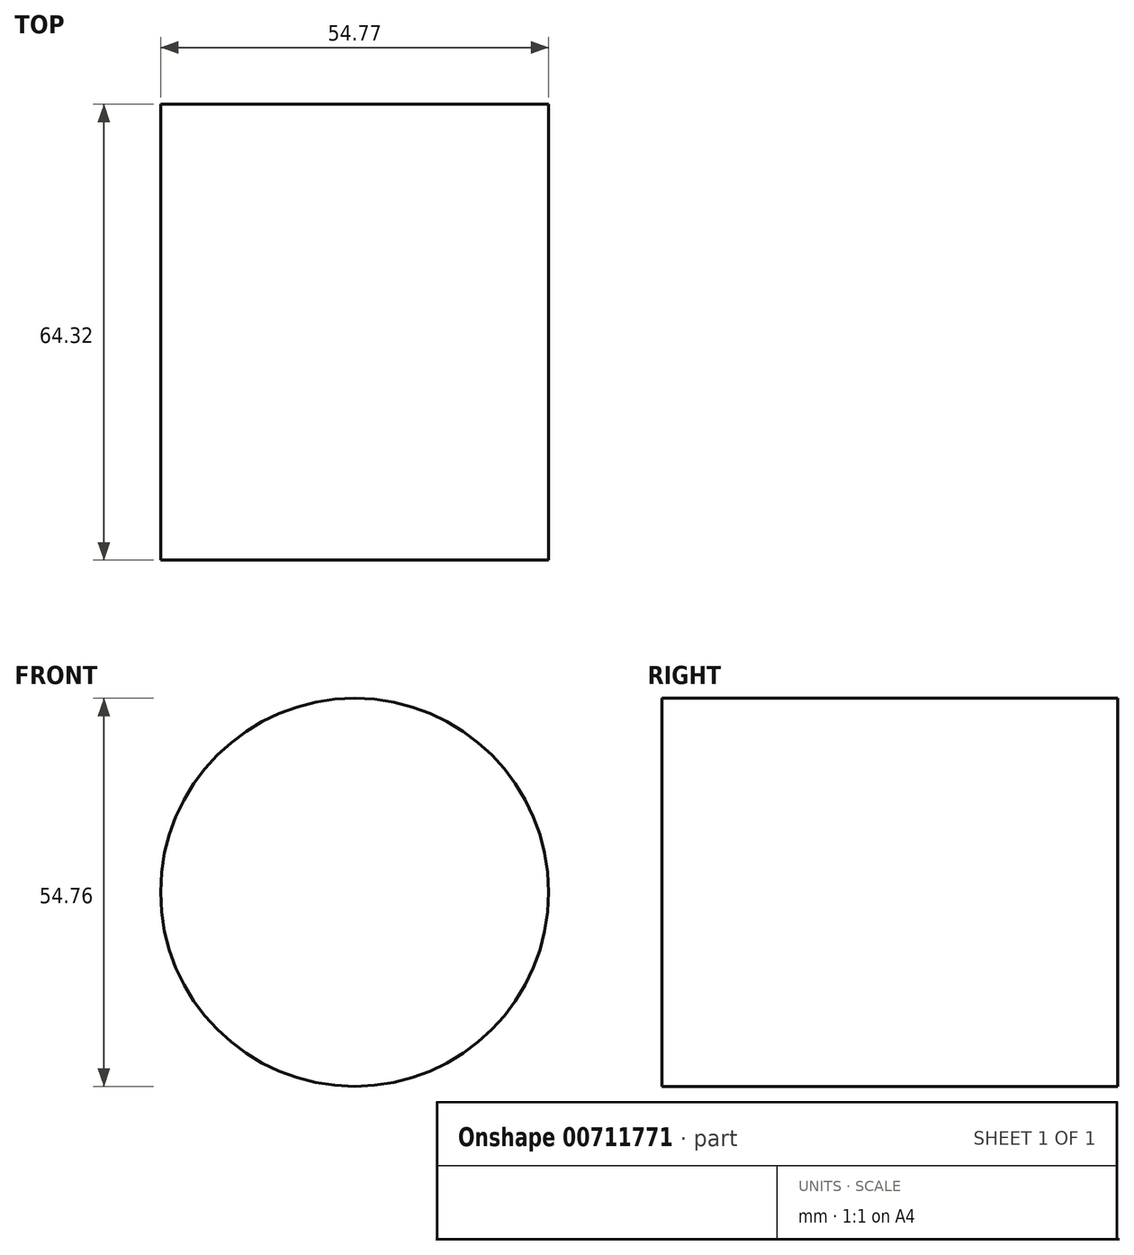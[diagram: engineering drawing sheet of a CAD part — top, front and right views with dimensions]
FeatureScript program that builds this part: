
annotation { "Feature Type Name" : "Feature", "Feature Type Description" : "" }
export const myFeature = defineFeature(function(context is Context, id is Id, definition is map)
    precondition{}
    {
        {
            var Q0;
            Q0=qCreatedBy(makeId("Top.planeOp"),FACE);
            var sketch = newSketch(context, id + "F0", { "sketchPlane" : qUnion([Q0])});
            skLineSegment(sketch, "E0.bottom", {"start": v(31.2, -24.15) * mm, "end": v(56.98, -24.15) * mm});
            skLineSegment(sketch, "E0.top", {"start": v(31.2, 44.87) * mm, "end": v(56.98, 44.87) * mm});
            skLineSegment(sketch, "E0.left", {"start": v(31.2, -24.15) * mm, "end": v(31.2, 44.87) * mm});
            skLineSegment(sketch, "E0.right", {"start": v(56.98, -24.15) * mm, "end": v(56.98, 44.87) * mm});
            skSolve(sketch);
        }
        {
            var Q0;
            Q0 = qSketchRegion(id + "F0", true);
            extrude(context, id + "F1", {"entities" : qUnion([Q0]), "depth" : 97.16 * mm, "offsetDistance" : 25.4 * mm});
        }
        {
            var Q0;
            Q0=makeQuery(id+"F1.opExtrude","SWEPT_FACE",FACE,{"disambiguationData":[OSD([sQuery(id+"F0.wireOp",EDGE,"E0.right")])]});
            var sketch = newSketch(context, id + "F2", { "sketchPlane" : qUnion([Q0])});
            skLineSegment(sketch, "E1.bottom", {"start": v(0, 81.33) * mm, "end": v(29.34, 81.33) * mm});
            skLineSegment(sketch, "E1.top", {"start": v(0, 13.33) * mm, "end": v(29.34, 13.33) * mm});
            skLineSegment(sketch, "E1.left", {"start": v(0, 81.33) * mm, "end": v(0, 13.33) * mm});
            skLineSegment(sketch, "E1.right", {"start": v(29.34, 81.33) * mm, "end": v(29.34, 13.33) * mm});
            skSolve(sketch);
        }
        {
            var Q0;
            Q0=makeQuery(id+"F2.imprint","IMPRINT",FACE,{"disambiguationData":[TD([[makeQuery(id+"F2.imprint","IMPRINT",EDGE,{"derivedFrom":sQuery(id+"F2.wireOp",EDGE,"E1.bottom")}),-1.0]])]});
            extrude(context, id + "F3", {"entities" : qUnion([Q0]), "operationType" : NewBodyOperationType.ADD, "oppositeDirection" : true, "depth" : 74.84 * mm, "offsetDistance" : 25.4 * mm});
        }
        {
            var Q0;
            Q0=makeQuery(id+"F1.opExtrude","SWEPT_BODY",BODY,{"disambiguationData":[OSD([sQuery(id+"F0.wireOp",EDGE,"E0.bottom"),sQuery(id+"F0.wireOp",EDGE,"E0.top"),sQuery(id+"F0.wireOp",EDGE,"E0.left"),sQuery(id+"F0.wireOp",EDGE,"E0.right")])]});
            deleteBodies(context, id + "F4", {"entities" : qUnion([Q0])});
        }
        {
            var Q0;
            Q0=qCreatedBy(makeId("Top.planeOp"),FACE);
            var sketch = newSketch(context, id + "F5", { "sketchPlane" : qUnion([Q0])});
            skLineSegment(sketch, "E2.bottom", {"start": v(-41.08, 32.99) * mm, "end": v(-13.7, 32.99) * mm});
            skLineSegment(sketch, "E2.top", {"start": v(-41.08, -31.33) * mm, "end": v(-13.7, -31.33) * mm});
            skLineSegment(sketch, "E2.left", {"start": v(-41.08, 32.99) * mm, "end": v(-41.08, -31.33) * mm});
            skLineSegment(sketch, "E2.right", {"start": v(-13.7, 32.99) * mm, "end": v(-13.7, -31.33) * mm});
            skSolve(sketch);
        }
        {
            var Q0;
            Q0=makeQuery(id+"F5.imprint","IMPRINT",FACE,{"disambiguationData":[TD([[makeQuery(id+"F5.imprint","IMPRINT",EDGE,{"derivedFrom":sQuery(id+"F5.wireOp",EDGE,"E2.bottom")}),-1.0]])]});
            var Q1;
            Q1=sQuery(id+"F5.wireOp",EDGE,"E2.right");
            revolve(context, id + "F6", {"surfaceOperationType" : NewSurfaceOperationType.NEW, "entities" : qUnion([Q0]), "axis" : qUnion([Q1]), "revolveType" : RevolveType.FULL});
        }
    });
